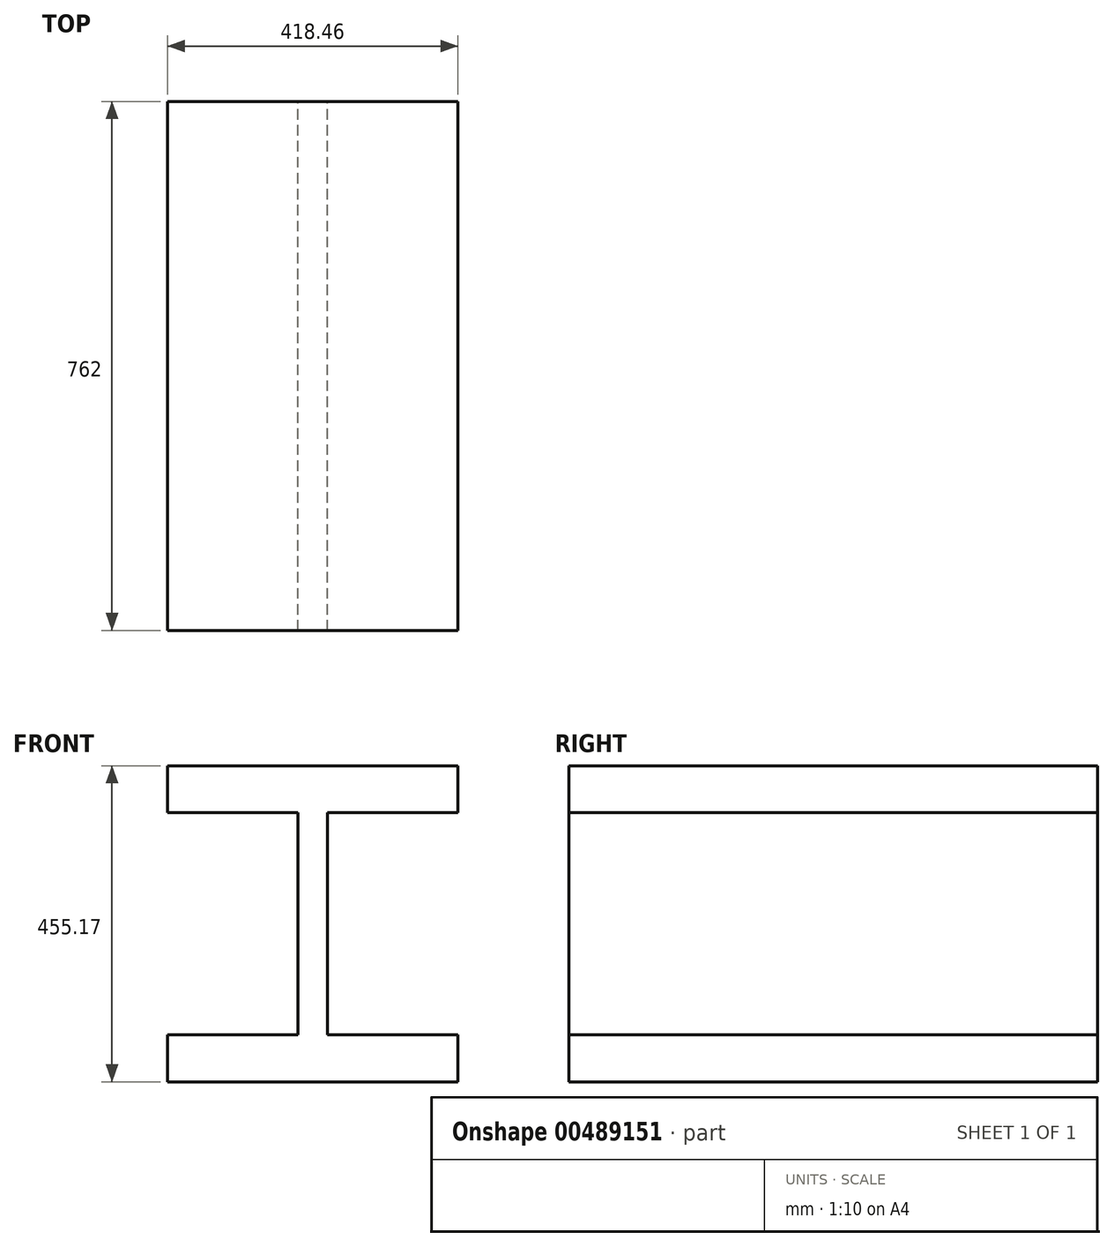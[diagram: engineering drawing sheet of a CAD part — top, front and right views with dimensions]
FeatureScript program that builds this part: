
annotation { "Feature Type Name" : "Feature", "Feature Type Description" : "" }
export const myFeature = defineFeature(function(context is Context, id is Id, definition is map)
    precondition{}
    {
        {
            var Q0;
            Q0=qCreatedBy(makeId("Front.planeOp"),FACE);
            var sketch = newSketch(context, id + "F0", { "sketchPlane" : qUnion([Q0])});
            skLineSegment(sketch, "E0", {"start": v(-230.62, 183.63) * mm, "end": v(0, 183.63) * mm});
            skLineSegment(sketch, "E1", {"start": v(0, 183.63) * mm, "end": v(187.84, 183.63) * mm});
            skLineSegment(sketch, "E2", {"start": v(187.84, 183.63) * mm, "end": v(187.84, 116.07) * mm});
            skLineSegment(sketch, "E3", {"start": v(187.84, 116.07) * mm, "end": v(-0.37, 116.07) * mm});
            skLineSegment(sketch, "E4", {"start": v(-0.37, 116.07) * mm, "end": v(-0.37, -203.97) * mm});
            skLineSegment(sketch, "E5", {"start": v(-0.37, -203.97) * mm, "end": v(187.84, -203.97) * mm});
            skLineSegment(sketch, "E6", {"start": v(187.84, -203.97) * mm, "end": v(187.84, -271.54) * mm});
            skLineSegment(sketch, "E7", {"start": v(187.84, -271.54) * mm, "end": v(0, -271.54) * mm});
            skLineSegment(sketch, "E8", {"start": v(0, -271.54) * mm, "end": v(-230.62, -271.54) * mm});
            skLineSegment(sketch, "E9", {"start": v(-230.62, -271.54) * mm, "end": v(-230.62, -203.97) * mm});
            skLineSegment(sketch, "E10", {"start": v(-230.62, -203.97) * mm, "end": v(-42.4, -203.97) * mm});
            skLineSegment(sketch, "E11", {"start": v(-42.4, -203.97) * mm, "end": v(-42.4, 116.07) * mm});
            skPoint(sketch, "E11.endSnap0", {"position": v(93.74, 116.07) * mm});
            skLineSegment(sketch, "E12", {"start": v(-42.4, 116.07) * mm, "end": v(-230.62, 116.07) * mm});
            skLineSegment(sketch, "E13", {"start": v(-230.62, 116.07) * mm, "end": v(-230.62, 183.63) * mm});
            skSolve(sketch);
        }
        {
            var Q0;
            Q0 = qSketchRegion(id + "F0", true);
            extrude(context, id + "F1", {"entities" : qUnion([Q0]), "depth" : 762 * mm});
        }
    });
